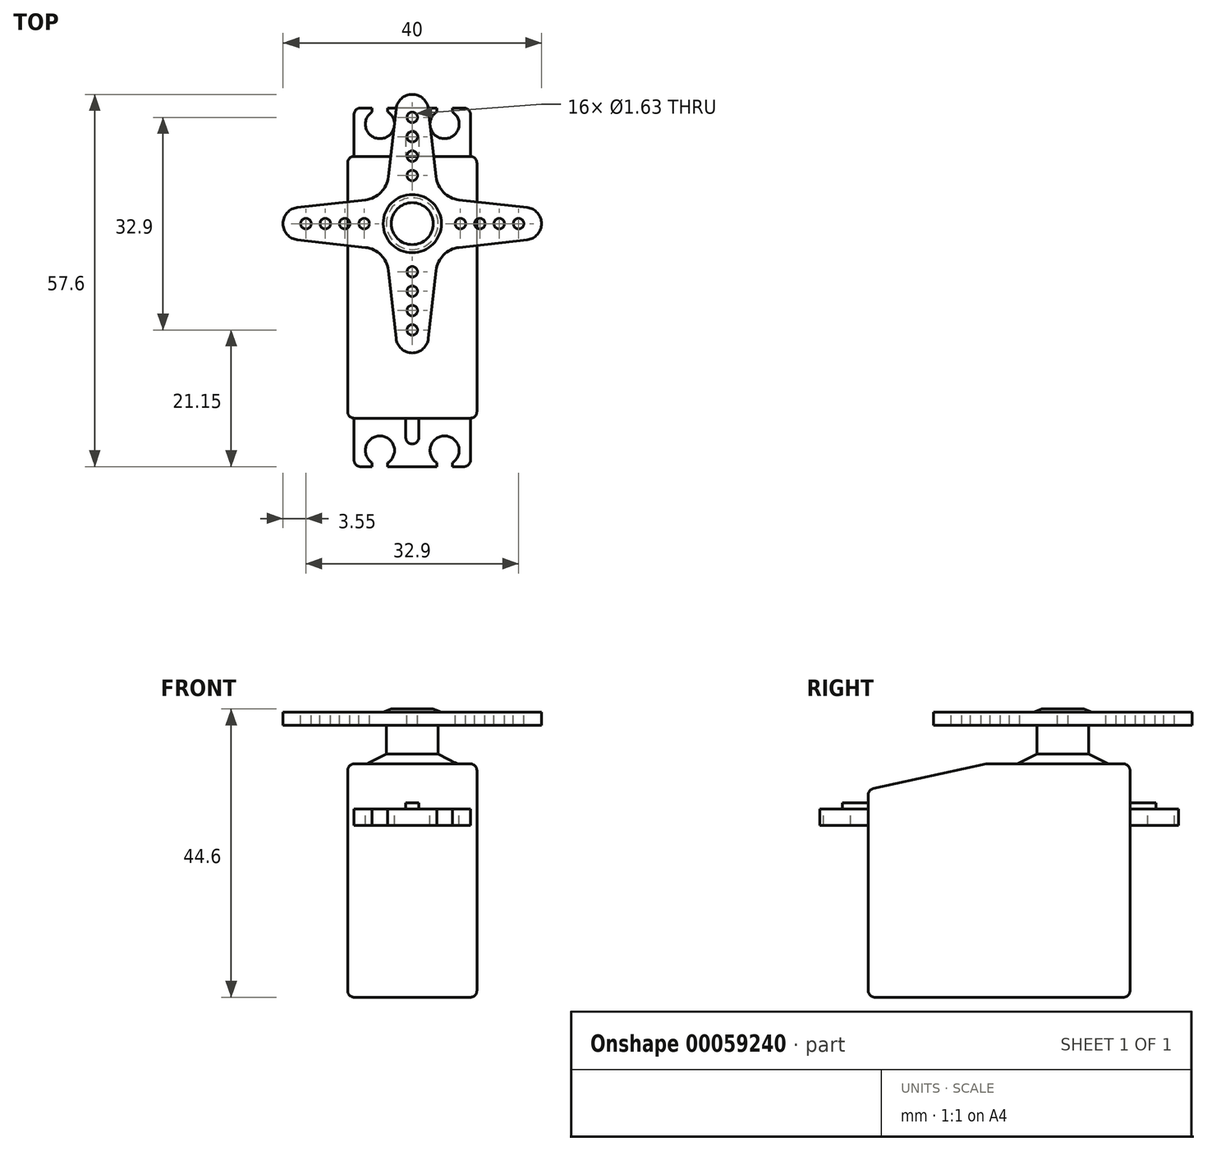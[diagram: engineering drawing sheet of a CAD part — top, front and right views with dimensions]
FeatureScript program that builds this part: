
annotation { "Feature Type Name" : "Feature", "Feature Type Description" : "" }
export const myFeature = defineFeature(function(context is Context, id is Id, definition is map)
    precondition{}
    {
        {
            var Q0;
            Q0=qCreatedBy(makeId("Right.planeOp"),FACE);
            var sketch = newSketch(context, id + "F0", { "sketchPlane" : qUnion([Q0])});
            skLineSegment(sketch, "E0.bottom", {"start": v(-20.25, 0) * mm, "end": v(20.25, 0) * mm});
            skLineSegment(sketch, "E0.top", {"start": v(-20.25, 36.1) * mm, "end": v(20.25, 36.1) * mm});
            skLineSegment(sketch, "E0.left", {"start": v(-20.25, 0) * mm, "end": v(-20.25, 36.1) * mm});
            skLineSegment(sketch, "E0.right", {"start": v(20.25, 0) * mm, "end": v(20.25, 36.1) * mm});
            skLineSegment(sketch, "E1.bottom", {"start": v(20.25, 29.1) * mm, "end": v(27.75, 29.1) * mm});
            skLineSegment(sketch, "E1.top", {"start": v(20.25, 26.6) * mm, "end": v(27.75, 26.6) * mm});
            skLineSegment(sketch, "E1.left", {"start": v(20.25, 29.1) * mm, "end": v(20.25, 26.6) * mm});
            skLineSegment(sketch, "E1.right", {"start": v(27.75, 29.1) * mm, "end": v(27.75, 26.6) * mm});
            skLineSegment(sketch, "E2.bottom", {"start": v(0, 36.1) * mm, "end": v(0, 36.1) * mm});
            skLineSegment(sketch, "E2.top", {"start": v(0, 0) * mm, "end": v(0, 0) * mm});
            skLineSegment(sketch, "E2.left", {"start": v(0, 36.1) * mm, "end": v(0, 0) * mm, "construction": true});
            skLineSegment(sketch, "E2.right", {"start": v(0, 36.1) * mm, "end": v(0, 0) * mm, "construction": true});
            skLineSegment(sketch, "E3.MirrorCS", {"start": v(-20.25, 29.1) * mm, "end": v(-27.75, 29.1) * mm});
            skLineSegment(sketch, "E4.MirrorCS", {"start": v(-27.75, 29.1) * mm, "end": v(-27.75, 26.6) * mm});
            skLineSegment(sketch, "E5.MirrorCS", {"start": v(-20.25, 26.6) * mm, "end": v(-27.75, 26.6) * mm});
            skLineSegment(sketch, "E6.MirrorCS", {"start": v(-20.25, 29.1) * mm, "end": v(-20.25, 26.6) * mm});
            skLineSegment(sketch, "E7", {"start": v(-20.25, 32.1) * mm, "end": v(-1.95, 36.1) * mm});
            skSolve(sketch);
        }
        {
            var Q0;
            {var subQ3=sQuery(id+"F0.wireOp",EDGE,"E0.bottom");Q0=makeQuery(id+"F0.imprint","IMPRINT",FACE,{"disambiguationData":[TD([[makeQuery(id+"F0.imprint","IMPRINT",EDGE,{"derivedFrom":subQ3}),1.0]])]});}
            extrude(context, id + "F1", {"entities" : qUnion([Q0]), "endBound" : BoundingType.SYMMETRIC, "depth" : 20 * mm, "hasSecondDirection" : true, "secondDirectionOppositeDirection" : true, "secondDirectionDepth" : 25 * mm});
        }
        {
            var Q0;
            Q0=makeQuery(id+"F0.imprint","IMPRINT",FACE,{"disambiguationData":[TD([[makeQuery(id+"F0.imprint","IMPRINT",EDGE,{"derivedFrom":sQuery(id+"F0.wireOp",EDGE,"E3.MirrorCS")}),1.0]])]});
            var Q1;
            Q1=makeQuery(id+"F0.imprint","IMPRINT",FACE,{"disambiguationData":[TD([[makeQuery(id+"F0.imprint","IMPRINT",EDGE,{"derivedFrom":sQuery(id+"F0.wireOp",EDGE,"E1.bottom")}),-1.0]])]});
            extrude(context, id + "F2", {"entities" : qUnion([Q0, Q1]), "operationType" : NewBodyOperationType.ADD, "endBound" : BoundingType.SYMMETRIC, "depth" : 18 * mm});
        }
        {
            var Q0;
            Q0=makeQuery(id+"F2.opExtrude","SWEPT_FACE",FACE,{"disambiguationData":[OSD([sQuery(id+"F0.wireOp",EDGE,"E3.MirrorCS")])]});
            var sketch = newSketch(context, id + "F3", { "sketchPlane" : qUnion([Q0])});
            skLineSegment(sketch, "E8.0", {"start": v(-10, -20.25) * mm, "end": v(-10, -1.95) * mm, "construction": true});
            skLineSegment(sketch, "E9.0", {"start": v(-10, -1.95) * mm, "end": v(-10, 20.25) * mm, "construction": true});
            skLineSegment(sketch, "E10.0", {"start": v(10, 20.25) * mm, "end": v(-10, 20.25) * mm, "construction": true});
            skLineSegment(sketch, "E11.0", {"start": v(10, -1.95) * mm, "end": v(10, 20.25) * mm, "construction": true});
            skLineSegment(sketch, "E12.0", {"start": v(10, -20.25) * mm, "end": v(10, -1.95) * mm, "construction": true});
            skLineSegment(sketch, "E13.0", {"start": v(10, -20.25) * mm, "end": v(-10, -20.25) * mm, "construction": true});
            skLineSegment(sketch, "E14", {"start": v(-10, -20.25) * mm, "end": v(10, 20.25) * mm, "construction": true});
            skLineSegment(sketch, "E15", {"start": v(-10, 20.25) * mm, "end": v(10, -20.25) * mm, "construction": true});
            skLineSegment(sketch, "E16", {"start": v(-10, 0) * mm, "end": v(10, 0) * mm, "construction": true});
            skPoint(sketch, "E16.endSnap0", {"position": v(0, 0) * mm});
            skLineSegment(sketch, "E17", {"start": v(0, -20.25) * mm, "end": v(0, 20.25) * mm, "construction": true});
            skCircle(sketch, "E18", {"center": v(-5, -25.25) * mm, "radius": 2.25 * mm});
            skLineSegment(sketch, "E19", {"start": v(-6.2, -27.75) * mm, "end": v(-3.8, -27.75) * mm});
            skLineSegment(sketch, "E20", {"start": v(-3.8, -27.75) * mm, "end": v(-3.8, -27.15) * mm});
            skLineSegment(sketch, "E21", {"start": v(-6.2, -27.75) * mm, "end": v(-6.2, -27.15) * mm});
            skLineSegment(sketch, "E22.MirrorCS", {"start": v(-6.2, 27.75) * mm, "end": v(-6.2, 27.15) * mm});
            skLineSegment(sketch, "E23.MirrorCS", {"start": v(-6.2, 27.75) * mm, "end": v(-3.8, 27.75) * mm});
            skLineSegment(sketch, "E24.MirrorCS", {"start": v(-3.8, 27.75) * mm, "end": v(-3.8, 27.15) * mm});
            skCircle(sketch, "E25.MirrorC", {"center": v(-5, 25.25) * mm, "radius": 2.25 * mm});
            skLineSegment(sketch, "E26.MirrorCS", {"start": v(3.8, -27.75) * mm, "end": v(3.8, -27.15) * mm});
            skLineSegment(sketch, "E27.MirrorCS", {"start": v(3.8, 27.75) * mm, "end": v(3.8, 27.15) * mm});
            skLineSegment(sketch, "E28.MirrorCS", {"start": v(6.2, 27.75) * mm, "end": v(6.2, 27.15) * mm});
            skLineSegment(sketch, "E29.MirrorCS", {"start": v(6.2, -27.75) * mm, "end": v(6.2, -27.15) * mm});
            skLineSegment(sketch, "E30.MirrorCS", {"start": v(6.2, 27.75) * mm, "end": v(3.8, 27.75) * mm});
            skLineSegment(sketch, "E31.MirrorCS", {"start": v(6.2, -27.75) * mm, "end": v(3.8, -27.75) * mm});
            skCircle(sketch, "E32.MirrorC", {"center": v(5, 25.25) * mm, "radius": 2.25 * mm});
            skCircle(sketch, "E33.MirrorC", {"center": v(5, -25.25) * mm, "radius": 2.25 * mm});
            skSolve(sketch);
        }
        {
            var Q0;
            Q0 = qSketchRegion(id + "F3", true);
            extrude(context, id + "F4", {"entities" : qUnion([Q0]), "operationType" : NewBodyOperationType.REMOVE, "oppositeDirection" : true, "depth" : 25 * mm});
        }
        {
            var Q0;
            Q0=makeQuery(id+"F2.opExtrude","SWEPT_FACE",FACE,{"disambiguationData":[OSD([sQuery(id+"F0.wireOp",EDGE,"E3.MirrorCS")])]});
            var sketch = newSketch(context, id + "F5", { "sketchPlane" : qUnion([Q0])});
            skLineSegment(sketch, "E34.0", {"start": v(10, -20.25) * mm, "end": v(-10, -20.25) * mm, "construction": true});
            skLineSegment(sketch, "E35.0", {"start": v(10, 20.25) * mm, "end": v(-10, 20.25) * mm, "construction": true});
            skLineSegment(sketch, "E36", {"start": v(0, -20.25) * mm, "end": v(0, 20.25) * mm, "construction": true});
            skLineSegment(sketch, "E37.rect.bottom", {"start": v(1, 23.25) * mm, "end": v(-1, 23.25) * mm});
            skLineSegment(sketch, "E37.rect.top", {"start": v(1, -23.25) * mm, "end": v(-1, -23.25) * mm});
            skLineSegment(sketch, "E37.rect.left", {"start": v(1, 23.25) * mm, "end": v(1, -23.25) * mm});
            skLineSegment(sketch, "E37.rect.right", {"start": v(-1, 23.25) * mm, "end": v(-1, -23.25) * mm});
            skPoint(sketch, "E37.rect.middle", {"position": v(0, 0) * mm});
            skArc(sketch, "E38", {"start": v(1, 23.25) * mm, "mid": v(0, 24.25) * mm, "end": v(-1, 23.25) * mm});
            skArc(sketch, "E39", {"start": v(-1, -23.25) * mm, "mid": v(0, -24.25) * mm, "end": v(1, -23.25) * mm});
            skPoint(sketch, "E40", {"position": v(0, 24.25) * mm});
            skSolve(sketch);
        }
        {
            var Q0;
            Q0 = qSketchRegion(id + "F5", true);
            extrude(context, id + "F6", {"entities" : qUnion([Q0]), "operationType" : NewBodyOperationType.ADD, "depth" : 1 * mm});
        }
        {
            var Q0;
            Q0=qCreatedBy(makeId("Right.planeOp"),FACE);
            var sketch = newSketch(context, id + "F7", { "sketchPlane" : qUnion([Q0])});
            skLineSegment(sketch, "E41.0", {"start": v(-1.95, 36.1) * mm, "end": v(20.25, 36.1) * mm, "construction": true});
            skLineSegment(sketch, "E42.0", {"start": v(-20.25, 0) * mm, "end": v(-20.25, 32.1) * mm, "construction": true});
            skLineSegment(sketch, "E43.0", {"start": v(20.25, 0) * mm, "end": v(20.25, 36.1) * mm, "construction": true});
            skLineSegment(sketch, "E44", {"start": v(9.85, 53.58) * mm, "end": v(9.85, 24.34) * mm, "construction": true});
            skLineSegment(sketch, "E45", {"start": v(16.85, 36.1) * mm, "end": v(13.85, 37.6) * mm});
            skLineSegment(sketch, "E46", {"start": v(13.85, 37.6) * mm, "end": v(13.85, 42.1) * mm});
            skLineSegment(sketch, "E47", {"start": v(13.85, 42.1) * mm, "end": v(29.85, 42.1) * mm});
            skLineSegment(sketch, "E48", {"start": v(29.85, 42.1) * mm, "end": v(29.85, 44.1) * mm});
            skLineSegment(sketch, "E49", {"start": v(29.85, 44.1) * mm, "end": v(14.35, 44.1) * mm});
            skLineSegment(sketch, "E50", {"start": v(14.35, 44.1) * mm, "end": v(13.1, 44.6) * mm});
            skLineSegment(sketch, "E51", {"start": v(13.1, 44.6) * mm, "end": v(9.85, 44.6) * mm});
            skLineSegment(sketch, "E52", {"start": v(9.85, 44.6) * mm, "end": v(9.85, 36.1) * mm});
            skLineSegment(sketch, "E53", {"start": v(9.85, 36.1) * mm, "end": v(16.85, 36.1) * mm});
            skSolve(sketch);
        }
        {
            var Q0;
            Q0 = qSketchRegion(id + "F7", true);
            var Q1;
            Q1=sQuery(id+"F7.wireOp",EDGE,"E44");
            revolve(context, id + "F8", {"operationType" : NewBodyOperationType.ADD, "entities" : qUnion([Q0]), "axis" : qUnion([Q1]), "revolveType" : RevolveType.FULL});
        }
        {
            var Q0;
            Q0=makeQuery(id+"F8.opRevolve","SWEPT_FACE",FACE,{"disambiguationData":[OSD([sQuery(id+"F7.wireOp",EDGE,"E49")])]});
            var sketch = newSketch(context, id + "F9", { "sketchPlane" : qUnion([Q0])});
            skPoint(sketch, "E54", {"position": v(0, 9.85) * mm});
            skCircle(sketch, "E55", {"center": v(0, 17.3) * mm, "radius": 0.81 * mm});
            skCircle(sketch, "E56", {"center": v(0, 20.3) * mm, "radius": 0.81 * mm});
            skCircle(sketch, "E57", {"center": v(0, 23.3) * mm, "radius": 0.81 * mm});
            skCircle(sketch, "E58", {"center": v(0, 26.3) * mm, "radius": 0.81 * mm});
            skCircle(sketch, "E59.1.0", {"center": v(-16.45, 9.85) * mm, "radius": 0.81 * mm});
            skCircle(sketch, "E59.1.1", {"center": v(-13.45, 9.85) * mm, "radius": 0.81 * mm});
            skCircle(sketch, "E59.1.2", {"center": v(-10.45, 9.85) * mm, "radius": 0.81 * mm});
            skCircle(sketch, "E59.1.3", {"center": v(-7.45, 9.85) * mm, "radius": 0.81 * mm});
            skCircle(sketch, "E59.2.0", {"center": v(0, -6.6) * mm, "radius": 0.81 * mm});
            skCircle(sketch, "E59.2.1", {"center": v(0, -3.6) * mm, "radius": 0.81 * mm});
            skCircle(sketch, "E59.2.2", {"center": v(0, -0.6) * mm, "radius": 0.81 * mm});
            skCircle(sketch, "E59.2.3", {"center": v(0, 2.4) * mm, "radius": 0.81 * mm});
            skCircle(sketch, "E59.3.0", {"center": v(16.45, 9.85) * mm, "radius": 0.81 * mm});
            skCircle(sketch, "E59.3.1", {"center": v(13.45, 9.85) * mm, "radius": 0.81 * mm});
            skCircle(sketch, "E59.3.2", {"center": v(10.45, 9.85) * mm, "radius": 0.81 * mm});
            skCircle(sketch, "E59.3.3", {"center": v(7.45, 9.85) * mm, "radius": 0.81 * mm});
            skSolve(sketch);
        }
        {
            var Q0;
            Q0 = qSketchRegion(id + "F9", true);
            extrude(context, id + "F10", {"entities" : qUnion([Q0]), "operationType" : NewBodyOperationType.REMOVE, "endBound" : BoundingType.UP_TO_NEXT, "oppositeDirection" : true, "depth" : 25 * mm});
        }
        {
            var Q0;
            Q0=makeQuery(id+"F8.opRevolve","SWEPT_FACE",FACE,{"disambiguationData":[OSD([sQuery(id+"F7.wireOp",EDGE,"E49")])]});
            var sketch = newSketch(context, id + "F11", { "sketchPlane" : qUnion([Q0])});
            skPoint(sketch, "E60", {"position": v(0, 9.85) * mm});
            skLineSegment(sketch, "E61", {"start": v(0, 9.85) * mm, "end": v(0, 29.85) * mm, "construction": true});
            skLineSegment(sketch, "E62", {"start": v(0, 9.85) * mm, "end": v(-14.14, 24) * mm, "construction": true});
            skLineSegment(sketch, "E63", {"start": v(0, 9.85) * mm, "end": v(14.14, 24) * mm, "construction": true});
            skLineSegment(sketch, "E64", {"start": v(-3.69, 17.1) * mm, "end": v(-2.5, 27.62) * mm});
            skArc(sketch, "E65", {"start": v(0, 29.85) * mm, "mid": v(-1.68, 29.21) * mm, "end": v(-2.5, 27.62) * mm});
            skArc(sketch, "E66", {"start": v(-4.84, 14.7) * mm, "mid": v(-4.06, 15.8) * mm, "end": v(-3.69, 17.1) * mm});
            skArc(sketch, "E67.MirrorCS", {"start": v(4.84, 14.7) * mm, "mid": v(4.06, 15.8) * mm, "end": v(3.69, 17.1) * mm});
            skLineSegment(sketch, "E68.MirrorCS", {"start": v(3.69, 17.1) * mm, "end": v(2.5, 27.62) * mm});
            skArc(sketch, "E69.MirrorCS", {"start": v(0, 29.85) * mm, "mid": v(1.68, 29.21) * mm, "end": v(2.5, 27.62) * mm});
            skArc(sketch, "E70.1.0", {"start": v(-4.84, 5) * mm, "mid": v(-5.95, 5.79) * mm, "end": v(-7.24, 6.16) * mm});
            skLineSegment(sketch, "E70.1.1", {"start": v(-7.24, 6.16) * mm, "end": v(-17.77, 7.35) * mm});
            skArc(sketch, "E70.1.2", {"start": v(-20, 9.85) * mm, "mid": v(-19.36, 8.17) * mm, "end": v(-17.77, 7.35) * mm});
            skArc(sketch, "E70.1.3", {"start": v(-20, 9.85) * mm, "mid": v(-19.36, 11.53) * mm, "end": v(-17.77, 12.35) * mm});
            skLineSegment(sketch, "E70.1.4", {"start": v(-7.24, 13.54) * mm, "end": v(-17.77, 12.35) * mm});
            skArc(sketch, "E70.1.5", {"start": v(-4.84, 14.7) * mm, "mid": v(-5.95, 13.91) * mm, "end": v(-7.24, 13.54) * mm});
            skArc(sketch, "E70.2.0", {"start": v(4.84, 5) * mm, "mid": v(4.06, 3.9) * mm, "end": v(3.69, 2.6) * mm});
            skLineSegment(sketch, "E70.2.1", {"start": v(3.69, 2.6) * mm, "end": v(2.5, -7.92) * mm});
            skArc(sketch, "E70.2.2", {"start": v(0, -10.15) * mm, "mid": v(1.68, -9.51) * mm, "end": v(2.5, -7.92) * mm});
            skArc(sketch, "E70.2.3", {"start": v(0, -10.15) * mm, "mid": v(-1.68, -9.51) * mm, "end": v(-2.5, -7.92) * mm});
            skLineSegment(sketch, "E70.2.4", {"start": v(-3.69, 2.6) * mm, "end": v(-2.5, -7.92) * mm});
            skArc(sketch, "E70.2.5", {"start": v(-4.84, 5) * mm, "mid": v(-4.06, 3.9) * mm, "end": v(-3.69, 2.6) * mm});
            skArc(sketch, "E70.3.0", {"start": v(4.84, 14.7) * mm, "mid": v(5.95, 13.91) * mm, "end": v(7.24, 13.54) * mm});
            skLineSegment(sketch, "E70.3.1", {"start": v(7.24, 13.54) * mm, "end": v(17.77, 12.35) * mm});
            skArc(sketch, "E70.3.2", {"start": v(20, 9.85) * mm, "mid": v(19.36, 11.53) * mm, "end": v(17.77, 12.35) * mm});
            skArc(sketch, "E70.3.3", {"start": v(20, 9.85) * mm, "mid": v(19.36, 8.17) * mm, "end": v(17.77, 7.35) * mm});
            skLineSegment(sketch, "E70.3.4", {"start": v(7.24, 6.16) * mm, "end": v(17.77, 7.35) * mm});
            skArc(sketch, "E70.3.5", {"start": v(4.84, 5) * mm, "mid": v(5.95, 5.79) * mm, "end": v(7.24, 6.16) * mm});
            skCircle(sketch, "E71", {"center": v(0, 9.85) * mm, "radius": 26.3 * mm});
            skSolve(sketch);
        }
        {
            var Q0;
            Q0 = qSketchRegion(id + "F11", true);
            var Q1;
            Q1=makeQuery(id+"F8.opRevolve","SWEPT_FACE",FACE,{"disambiguationData":[OSD([sQuery(id+"F7.wireOp",EDGE,"E47")])]});
            extrude(context, id + "F12", {"entities" : qUnion([Q0]), "operationType" : NewBodyOperationType.REMOVE, "endBound" : BoundingType.UP_TO_SURFACE, "oppositeDirection" : true, "endBoundEntityFace" : qUnion([Q1]), "depth" : 25 * mm});
        }
        {
            var Q0;
            Q0=makeQuery(id+"F1.opExtrude","CAP_FACE",FACE,{"disambiguationData":[OSD([sQuery(id+"F0.wireOp",EDGE,"E0.bottom"),sQuery(id+"F0.wireOp",EDGE,"E0.top"),sQuery(id+"F0.wireOp",EDGE,"E0.left"),sQuery(id+"F0.wireOp",EDGE,"E0.right"),sQuery(id+"F0.wireOp",EDGE,"E1.left"),sQuery(id+"F0.wireOp",EDGE,"E6.MirrorCS"),sQuery(id+"F0.wireOp",EDGE,"E7")])],"isStart":false});
            var Q1;
            Q1=makeQuery(id+"F1.opExtrude","CAP_FACE",FACE,{"disambiguationData":[OSD([sQuery(id+"F0.wireOp",EDGE,"E0.bottom"),sQuery(id+"F0.wireOp",EDGE,"E0.top"),sQuery(id+"F0.wireOp",EDGE,"E0.left"),sQuery(id+"F0.wireOp",EDGE,"E0.right"),sQuery(id+"F0.wireOp",EDGE,"E1.left"),sQuery(id+"F0.wireOp",EDGE,"E6.MirrorCS"),sQuery(id+"F0.wireOp",EDGE,"E7")])],"isStart":true});
            var Q2;
            Q2=makeQuery(id+"F1.opExtrude","SWEPT_FACE",FACE,{"disambiguationData":[OSD([sQuery(id+"F0.wireOp",EDGE,"E0.bottom")])]});
            var Q3;
            Q3=makeQuery(id+"F1.opExtrude","SWEPT_FACE",FACE,{"disambiguationData":[OSD([sQuery(id+"F0.wireOp",EDGE,"E7")])]});
            var Q4;
            Q4=makeQuery(id+"F1.opExtrude","SWEPT_FACE",FACE,{"disambiguationData":[OSD([sQuery(id+"F0.wireOp",EDGE,"E0.top")])]});
            var Q5;
            Q5=makeQuery(id+"F2.opExtrude","CAP_EDGE",EDGE,{"disambiguationData":[OSD([sQuery(id+"F0.wireOp",EDGE,"E4.MirrorCS")])],"isStart":false});
            var Q6;
            Q6=makeQuery(id+"F2.opExtrude","CAP_EDGE",EDGE,{"disambiguationData":[OSD([sQuery(id+"F0.wireOp",EDGE,"E4.MirrorCS")])],"isStart":true});
            var Q7;
            Q7=makeQuery(id+"F2.opExtrude","CAP_EDGE",EDGE,{"disambiguationData":[OSD([sQuery(id+"F0.wireOp",EDGE,"E1.right")])],"isStart":false});
            var Q8;
            Q8=makeQuery(id+"F2.opExtrude","CAP_EDGE",EDGE,{"disambiguationData":[OSD([sQuery(id+"F0.wireOp",EDGE,"E1.right")])],"isStart":true});
            fillet(context, id + "F13", {"entities" : qUnion([Q0, Q1, Q2, Q3, Q4, Q5, Q6, Q7, Q8]), "radius" : 1 * mm, "tangentPropagation" : true, "allowEdgeOverflow" : false});
        }
    });
